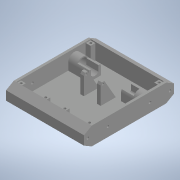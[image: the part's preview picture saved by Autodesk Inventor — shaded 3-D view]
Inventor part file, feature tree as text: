
AUTODESK INVENTOR PART (.ipt)
format: ipt  version: 2020 (Build 240168000, 168)  size: 390,144 bytes
history: native  units: in
note: dims shown in document units (in); Inventor stores cm internally (conversion verified against a paired STEP export)
features: projected_geometry x13, extrude x11, sketch x11, mirror x4, plane x1
ambient origin geometry x8: Origin, YZ Plane, XZ Plane, XY Plane, X Axis, Y Axis, Z Axis, Center Point
bodies: Solid1 (feature_tree)
feature tree (40):
  extrude  "Extrusion1"  Depth=5.9055in
  extrude  "Extrusion2"  TaperAngle=0.0deg  [1 undecoded]
  extrude  "Extrusion3"  Depth=1.063in
  extrude  "Extrusion4"  Depth=0.315in
  extrude  "Extrusion5"  TaperAngle=0.0deg  [1 undecoded]
  extrude  "Extrusion6"  Depth=0.5906in
  mirror  "Mirror1"
  extrude  "Extrusion7"  Depth=0.0787in
  mirror  "Mirror2"
  extrude  "Extrusion8"  Depth=0.5512in
  mirror  "Mirror3"
  plane  "Work Plane1"
  extrude  "Extrusion9"  Depth=0.7874in TaperAngle=0.0deg
  mirror  "Mirror4"
  extrude  "Extrusion10"  Depth=6.063in TaperAngle=0.0deg
  extrude  "Extrusion11"  Depth=0.1575in
  sketch  "Sketch1"  dims[d0=1.1811in d1=5.9055in]
  sketch  "Sketch2"  dims[d2=5.1181in d3=0.0in]
  projected_geometry  "Projected Loop1"
  sketch  "Sketch3"  dims[d4=0.1575in d5=1.063in]
  projected_geometry  "Projected Loop2"
  projected_geometry  "Projected Loop3"
  sketch  "Sketch4"  dims[d6=0.0in d8=0.315in]
  sketch  "Sketch5"  dims[d10=0.993in d11=0.0in]
  projected_geometry  "Projected Loop4"
  sketch  "Sketch6"  dims[d12=0.6496in d13=0.5906in]
  sketch  "Sketch7"  dims[d14=1.5748in d15=0.0787in]
  sketch  "Sketch9"  dims[d16=0.5512in d17=0.0in d18=0.6102in]
  sketch  "Sketch10"  dims[d19=0.4803in d20=0.7874in d21=0.0in]
  sketch  "Sketch12"  dims[d22=0.1654in d23=6.063in d24=0.0in]
  projected_geometry  "Projected Loop6"
  projected_geometry  "Projected Loop7"
  projected_geometry  "Projected Loop8"
  sketch  "Sketch13"  dims[d25=0.5114in d26=0.1575in d27=1.5748in d28=0.0in d29=0.0in d30=0.1575in d31=0.2756in d32=0.0in d33=0.4331in d34=0.122in d38=2.7559in d40=0.061in d41=0.0909in d42=0.2362in d43=0.0in d44=60.0deg d45=0.0787in d46=0.315in d48=0.993in d49=0.0in d51=0.1575in d52=0.1575in d53=0.2756in d54=0.0in d55=0.4724in]
  projected_geometry  "Projected Loop9"
  projected_geometry  "Projected Loop10"
  projected_geometry  "Projected Loop11"
  projected_geometry  "Projected Loop12"
  projected_geometry  "Projected Loop13"
  projected_geometry  "Projected Loop14"
note: 2 required parameter values undecoded (feature->parameter linkage not recoverable at this tier; creation-order binding heuristic only, values carry confidence <= 0.55)
